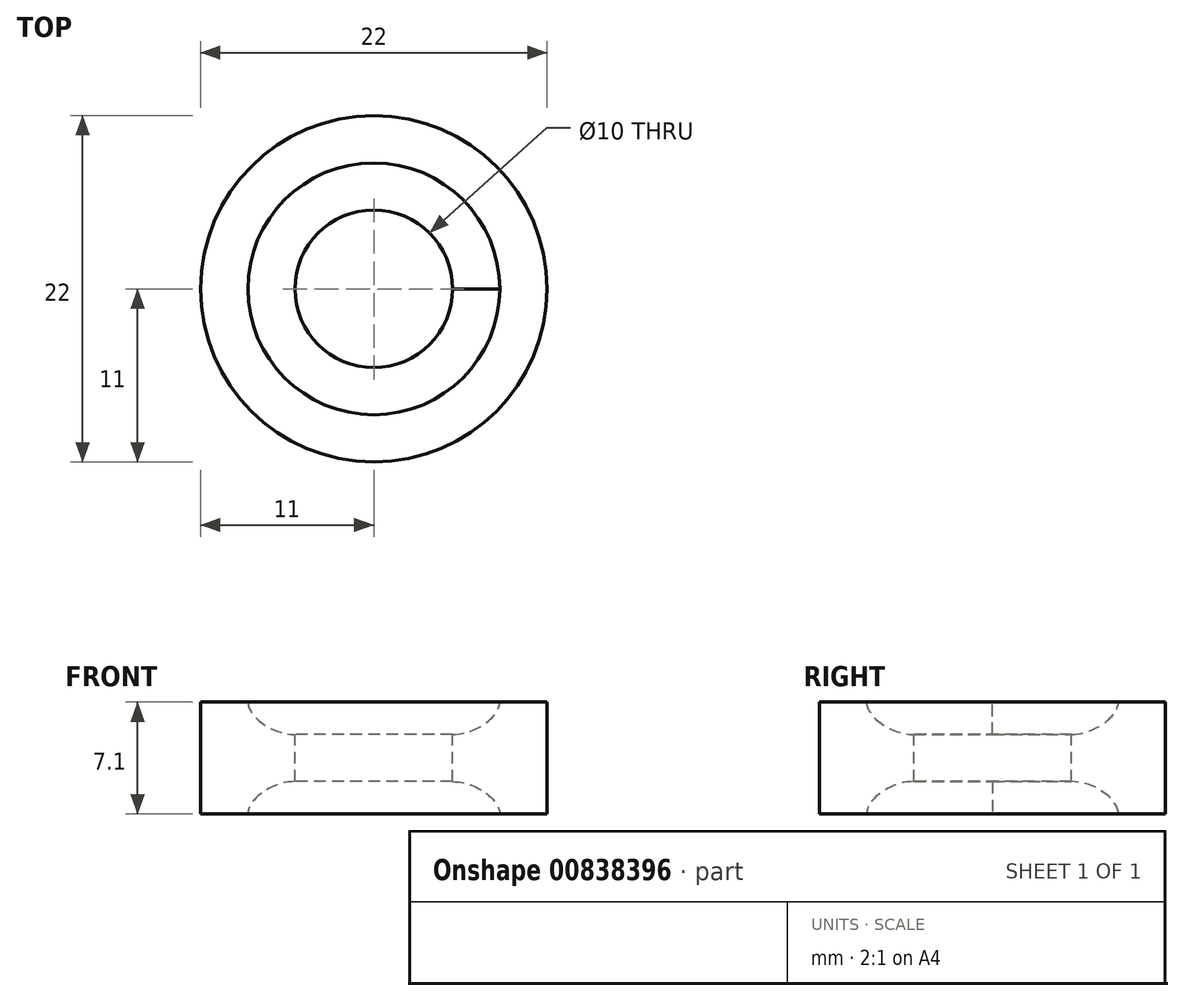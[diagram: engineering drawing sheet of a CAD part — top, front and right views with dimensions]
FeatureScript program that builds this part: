
annotation { "Feature Type Name" : "Feature", "Feature Type Description" : "" }
export const myFeature = defineFeature(function(context is Context, id is Id, definition is map)
    precondition{}
    {
        {
            var Q0;
            Q0=qCreatedBy(makeId("Front.planeOp"),FACE);
            var sketch = newSketch(context, id + "F0", { "sketchPlane" : qUnion([Q0])});
            skLineSegment(sketch, "E0", {"start": v(5, 1.5) * mm, "end": v(5, -1.5) * mm});
            skLineSegment(sketch, "E1", {"start": v(8, 3.55) * mm, "end": v(11, 3.55) * mm});
            skLineSegment(sketch, "E2", {"start": v(11, 3.55) * mm, "end": v(11, -3.55) * mm});
            skLineSegment(sketch, "E3", {"start": v(11, -3.55) * mm, "end": v(8, -3.55) * mm});
            skFitSpline(sketch, "E4", {"points": [v(5, 1.5) * mm, v(8, 3.55) * mm], "startDerivative": vector(4.61, 0) * mm, "endDerivative": vector(0, 2.62) * mm});
            skFitSpline(sketch, "E5", {"points": [v(5, -1.5) * mm, v(8, -3.55) * mm], "startDerivative": vector(4.61, 0) * mm, "endDerivative": vector(0, -2.62) * mm});
            skLineSegment(sketch, "E6", {"start": v(0, 1.56) * mm, "end": v(0, -2.72) * mm, "construction": true});
            skSolve(sketch);
        }
        {
            var Q0;
            Q0=makeQuery(id+"F0.imprint","IMPRINT",FACE,{"disambiguationData":[TD([[makeQuery(id+"F0.imprint","IMPRINT",EDGE,{"derivedFrom":sQuery(id+"F0.wireOp",EDGE,"E0")}),1.0]])]});
            var Q1;
            Q1=sQuery(id+"F0.wireOp",EDGE,"E6");
            revolve(context, id + "F1", {"surfaceOperationType" : NewSurfaceOperationType.NEW, "entities" : qUnion([Q0]), "axis" : qUnion([Q1]), "revolveType" : RevolveType.FULL});
        }
    });
